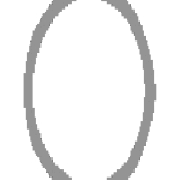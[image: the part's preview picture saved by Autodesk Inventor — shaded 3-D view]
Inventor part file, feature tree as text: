
AUTODESK INVENTOR PART (.ipt)
format: ipt  version: 2021 (Build 250183000, 183)  size: 142,336 bytes
history: native  units: in
note: dims shown in document units (in); Inventor stores cm internally (conversion verified against a paired STEP export)
features: plane x7, sketch x5, other x4, extrude x2, boolean_combine x2
ambient origin geometry x8: Origin, YZ Plane, XZ Plane, XY Plane, X Axis, Y Axis, Z Axis, Center Point
bodies: Solid1 (feature_tree), Body (feature_tree), Solid2 (feature_tree), Solid3 (feature_tree)
feature tree (20):
  other  "Driven Length"
  other  "Frame Generator"
  other  "Start Plane"
  other  "End Plane"
  plane  "Work Plane4"
  plane  "Work Plane5"
  plane  "Work Plane6"
  extrude  "Extrusion3"  Depth=0.065in
  boolean_combine  "Combine1"
  plane  "Work Plane7"
  plane  "Work Plane8"
  plane  "Work Plane9"
  extrude  "Extrusion4"  TaperAngle=0.0deg  [1 undecoded]
  boolean_combine  "Combine2"
  sketch  "Sketch"  dims[d8=90.0deg d9=5.831in d10=0.12in d11=0.0in d12=0.12in d13=0.0in]
  sketch  "Sketch2"  dims[d0=1.0in d1=0.065in]
  plane  "Work Plane3"
  sketch  "Sketch3"  dims[d2=5.831in d4=-0.0in]
  sketch  "Sketch4"  dims[d5=5.831in]
  sketch  "Sketch5"  dims[d6=0.12in d7=0.0in]
note: 1 required parameter value undecoded (feature->parameter linkage not recoverable at this tier; creation-order binding heuristic only, values carry confidence <= 0.55)
